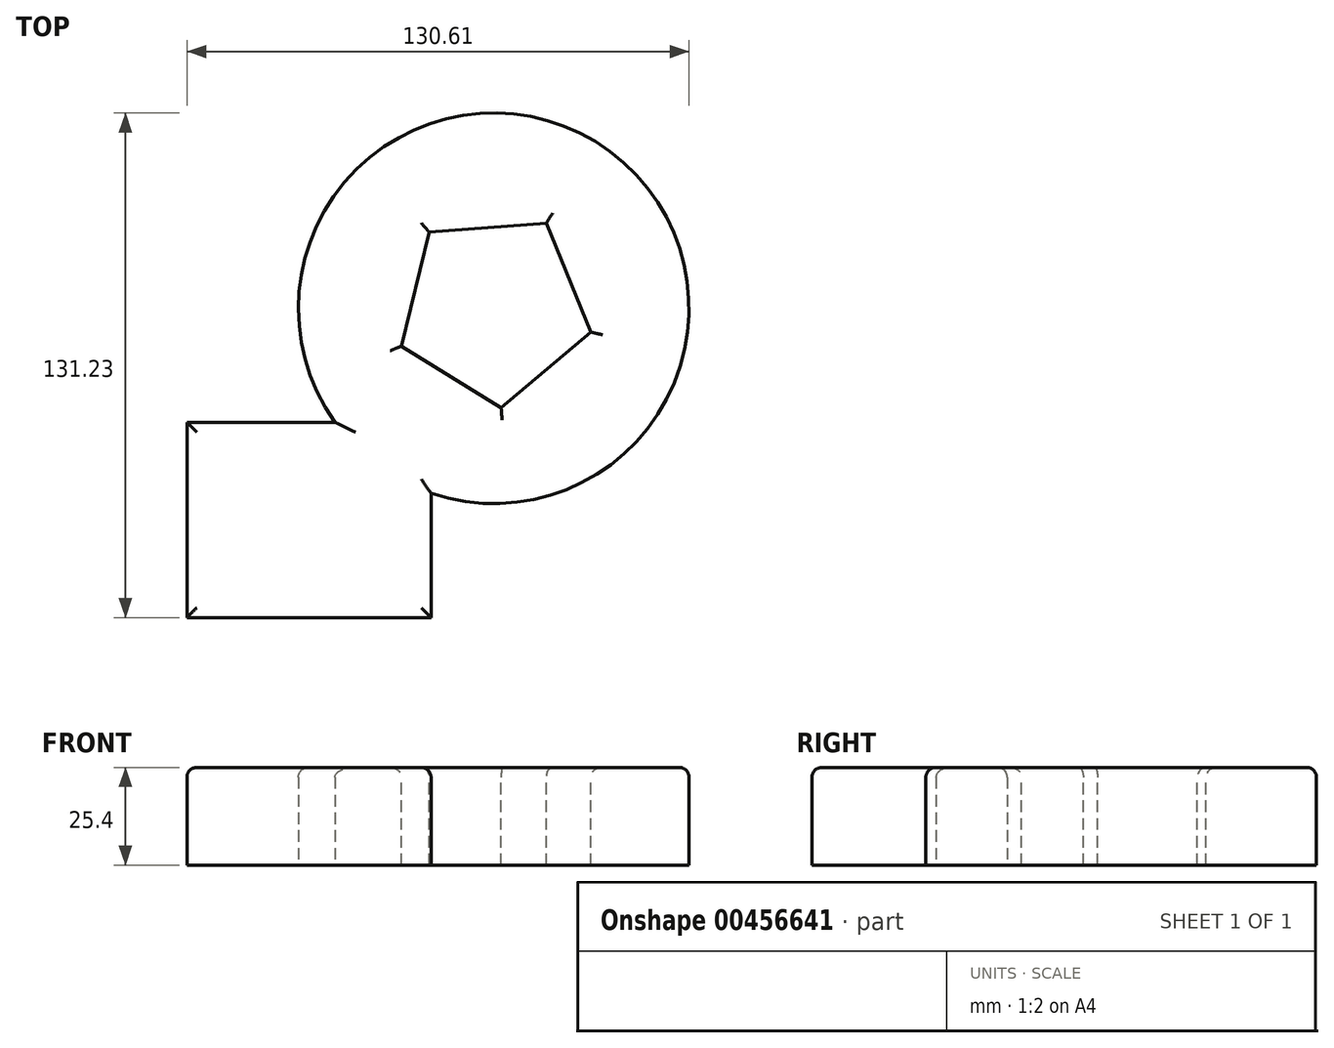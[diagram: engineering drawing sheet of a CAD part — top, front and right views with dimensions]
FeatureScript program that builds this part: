
annotation { "Feature Type Name" : "Feature", "Feature Type Description" : "" }
export const myFeature = defineFeature(function(context is Context, id is Id, definition is map)
    precondition{}
    {
        {
            var Q0;
            Q0=qCreatedBy(makeId("Top.planeOp"),FACE);
            var sketch = newSketch(context, id + "F0", { "sketchPlane" : qUnion([Q0])});
            skLineSegment(sketch, "E0", {"start": v(63.5, -50.8) * mm, "end": v(0, -50.8) * mm});
            skLineSegment(sketch, "E1", {"start": v(0, -50.8) * mm, "end": v(0, 0) * mm});
            skLineSegment(sketch, "E2", {"start": v(0, 0) * mm, "end": v(38.54, 0) * mm});
            skLineSegment(sketch, "E3", {"start": v(63.5, -18.48) * mm, "end": v(63.5, -50.8) * mm});
            skArc(sketch, "E4", {"start": v(63.5, -18.48) * mm, "mid": v(110.03, 70.46) * mm, "end": v(38.54, 0) * mm});
            skSolve(sketch);
        }
        {
            var Q0;
            Q0=makeQuery(id+"F0.imprint","IMPRINT",FACE,{"disambiguationData":[TD([[makeQuery(id+"F0.imprint","IMPRINT",EDGE,{"derivedFrom":sQuery(id+"F0.wireOp",EDGE,"E0")}),-1.0]])]});
            extrude(context, id + "F1", {"entities" : qUnion([Q0]), "depth" : 48.26 * mm});
        }
        {
            var Q0;
            Q0=makeQuery(id+"F1.opExtrude","CAP_FACE",FACE,{"disambiguationData":[OSD([sQuery(id+"F0.wireOp",EDGE,"E0"),sQuery(id+"F0.wireOp",EDGE,"E1"),sQuery(id+"F0.wireOp",EDGE,"E2"),sQuery(id+"F0.wireOp",EDGE,"E3"),sQuery(id+"F0.wireOp",EDGE,"E4")])],"isStart":false});
            var sketch = newSketch(context, id + "F2", { "sketchPlane" : qUnion([Q0])});
            skCircle(sketch, "E5.cCircle", {"center": v(79.8, 29.63) * mm, "radius": 21.02 * mm, "construction": true});
            skLineSegment(sketch, "E5.0", {"start": v(55.77, 19.78) * mm, "end": v(63, 49.45) * mm});
            skLineSegment(sketch, "E5.1", {"start": v(63, 49.45) * mm, "end": v(93.46, 51.74) * mm});
            skLineSegment(sketch, "E5.2", {"start": v(93.46, 51.74) * mm, "end": v(105.05, 23.48) * mm});
            skLineSegment(sketch, "E5.3", {"start": v(105.05, 23.48) * mm, "end": v(81.75, 3.73) * mm});
            skLineSegment(sketch, "E5.4", {"start": v(81.75, 3.73) * mm, "end": v(55.77, 19.78) * mm});
            skPoint(sketch, "E5.0.midPoint", {"position": v(59.38, 34.61) * mm});
            skSolve(sketch);
        }
        {
            var Q0;
            Q0=makeQuery(id+"F2.imprint","IMPRINT",FACE,{"disambiguationData":[TD([[makeQuery(id+"F2.imprint","IMPRINT",EDGE,{"derivedFrom":sQuery(id+"F2.wireOp",EDGE,"E5.0")}),1.0]])]});
            extrude(context, id + "F3", {"entities" : qUnion([Q0]), "operationType" : NewBodyOperationType.INTERSECT, "oppositeDirection" : true, "depth" : 25.4 * mm});
        }
        {
            var Q0;
            Q0=makeQuery(id+"F1.opExtrude","CAP_EDGE",EDGE,{"disambiguationData":[OSD([sQuery(id+"F0.wireOp",EDGE,"E4")])],"isStart":false});
            var Q1;
            Q1=makeQuery(id+"F1.opExtrude","CAP_EDGE",EDGE,{"disambiguationData":[OSD([sQuery(id+"F0.wireOp",EDGE,"E2")])],"isStart":false});
            var Q2;
            Q2=makeQuery(id+"F1.opExtrude","CAP_FACE",FACE,{"disambiguationData":[OSD([sQuery(id+"F0.wireOp",EDGE,"E0"),sQuery(id+"F0.wireOp",EDGE,"E1"),sQuery(id+"F0.wireOp",EDGE,"E2"),sQuery(id+"F0.wireOp",EDGE,"E3"),sQuery(id+"F0.wireOp",EDGE,"E4")])],"isStart":false});
            fillet(context, id + "F4", {"entities" : qUnion([Q0, Q1, Q2]), "radius" : 2.54 * mm, "tangentPropagation" : true, "allowEdgeOverflow" : false});
        }
        {
            var Q0;
            Q0=qCreatedBy(makeId("Front.planeOp"),FACE);
            var sketch = newSketch(context, id + "F5", { "sketchPlane" : qUnion([Q0])});
            skFitSpline(sketch, "E6", {"points": [v(21.85, 48.26) * mm, v(0, 103.03) * mm, v(-45.62, 135.18) * mm, v(-25.5, 160.93) * mm, v(-89.19, 226.7) * mm], "startDerivative": vector(67.36, 238.44) * mm, "endDerivative": vector(-391.71, 230.75) * mm});
            skSolve(sketch);
        }
        {
            var Q0;
            Q0=makeQuery(id+"F1.opExtrude","CAP_FACE",FACE,{"disambiguationData":[OSD([sQuery(id+"F0.wireOp",EDGE,"E0"),sQuery(id+"F0.wireOp",EDGE,"E1"),sQuery(id+"F0.wireOp",EDGE,"E2"),sQuery(id+"F0.wireOp",EDGE,"E3"),sQuery(id+"F0.wireOp",EDGE,"E4")])],"isStart":false});
            var sketch = newSketch(context, id + "F6", { "sketchPlane" : qUnion([Q0])});
            skCircle(sketch, "E7", {"center": v(21.96, 0) * mm, "radius": 8.32 * mm});
            skSolve(sketch);
        }
    });
